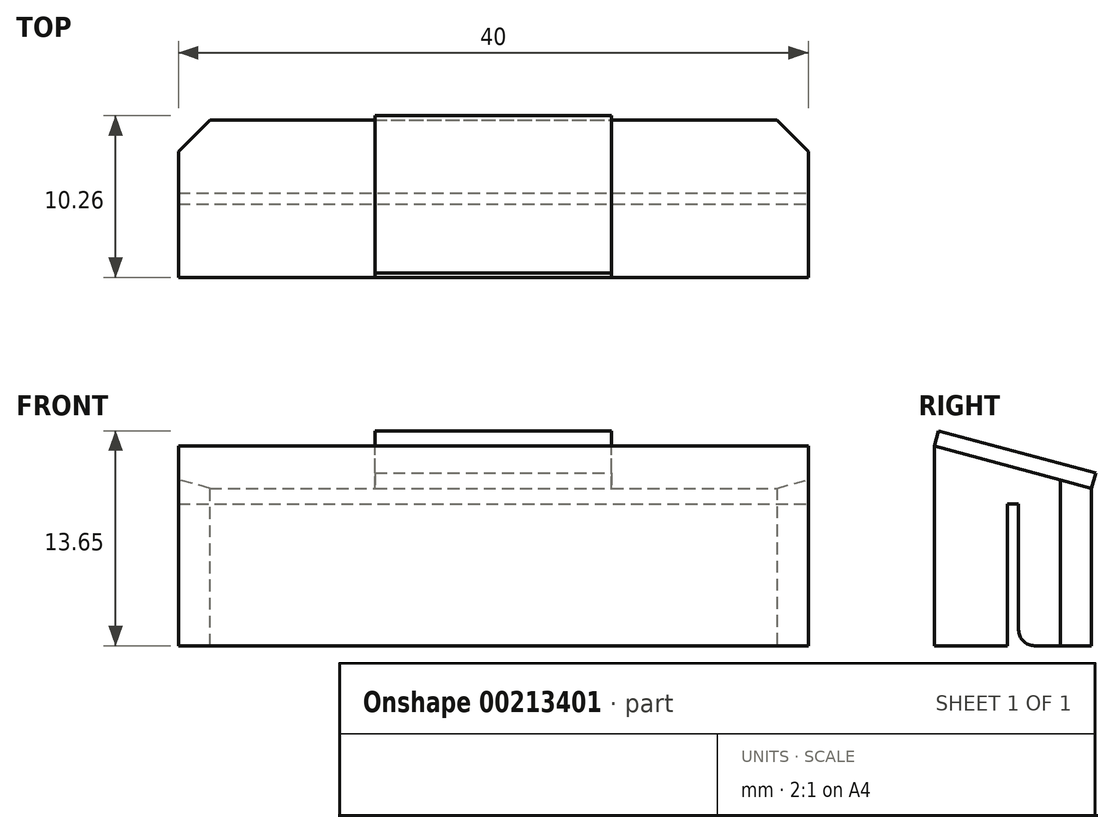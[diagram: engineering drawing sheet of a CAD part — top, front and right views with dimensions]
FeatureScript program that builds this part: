
annotation { "Feature Type Name" : "Feature", "Feature Type Description" : "" }
export const myFeature = defineFeature(function(context is Context, id is Id, definition is map)
    precondition{}
    {
        {
            var Q0;
            Q0=qCreatedBy(makeId("Top.planeOp"),FACE);
            var sketch = newSketch(context, id + "F0", { "sketchPlane" : qUnion([Q0])});
            skLineSegment(sketch, "E0.bottom", {"start": v(-20, 5) * mm, "end": v(20, 5) * mm});
            skLineSegment(sketch, "E0.top", {"start": v(-20, -5) * mm, "end": v(20, -5) * mm});
            skLineSegment(sketch, "E0.left", {"start": v(-20, 5) * mm, "end": v(-20, -5) * mm});
            skLineSegment(sketch, "E0.right", {"start": v(20, 5) * mm, "end": v(20, -5) * mm});
            skPoint(sketch, "E1", {"position": v(0, 5) * mm});
            skPoint(sketch, "E2", {"position": v(20, 0) * mm});
            skSolve(sketch);
        }
        {
            var Q0;
            Q0=makeQuery(id+"F0.imprint","IMPRINT",FACE,{"disambiguationData":[TD([[makeQuery(id+"F0.imprint","IMPRINT",EDGE,{"derivedFrom":sQuery(id+"F0.wireOp",EDGE,"E0.bottom")}),-1.0]])]});
            extrude(context, id + "F1", {"entities" : qUnion([Q0]), "depth" : 10 * mm});
        }
        {
            var Q0;
            Q0=makeQuery(id+"F1.opExtrude","SWEPT_FACE",FACE,{"disambiguationData":[OSD([sQuery(id+"F0.wireOp",EDGE,"E0.right")])]});
            var sketch = newSketch(context, id + "F2", { "sketchPlane" : qUnion([Q0])});
            skLineSegment(sketch, "E3", {"start": v(5, 10) * mm, "end": v(-5, 10) * mm});
            skLineSegment(sketch, "E4", {"start": v(-5, 10) * mm, "end": v(-5, 12.68) * mm});
            skLineSegment(sketch, "E5", {"start": v(-5, 12.68) * mm, "end": v(5, 10) * mm});
            skSolve(sketch);
        }
        {
            var Q0;
            Q0=makeQuery(id+"F2.imprint","IMPRINT",FACE,{"disambiguationData":[TD([[makeQuery(id+"F2.imprint","IMPRINT",EDGE,{"derivedFrom":sQuery(id+"F2.wireOp",EDGE,"E3")}),-1.0]])]});
            var Q1;
            Q1=makeQuery(id+"F1.opExtrude","SWEPT_FACE",FACE,{"disambiguationData":[OSD([sQuery(id+"F0.wireOp",EDGE,"E0.left")])]});
            extrude(context, id + "F3", {"entities" : qUnion([Q0]), "operationType" : NewBodyOperationType.ADD, "endBound" : BoundingType.UP_TO_SURFACE, "oppositeDirection" : true, "endBoundEntityFace" : qUnion([Q1]), "depth" : 25 * mm});
        }
        {
            var Q0;
            Q0=makeQuery(id+"F3.opExtrude","SWEPT_FACE",FACE,{"disambiguationData":[OSD([sQuery(id+"F2.wireOp",EDGE,"E5")])]});
            var sketch = newSketch(context, id + "F4", { "sketchPlane" : qUnion([Q0])});
            skLineSegment(sketch, "E6.bottom", {"start": v(-7.5, 2.24) * mm, "end": v(7.5, 2.24) * mm});
            skLineSegment(sketch, "E6.top", {"start": v(-7.5, -8.11) * mm, "end": v(7.5, -8.11) * mm});
            skLineSegment(sketch, "E6.left", {"start": v(-7.5, 2.24) * mm, "end": v(-7.5, -8.11) * mm});
            skLineSegment(sketch, "E6.right", {"start": v(7.5, 2.24) * mm, "end": v(7.5, -8.11) * mm});
            skPoint(sketch, "E7", {"position": v(0, 2.24) * mm});
            skSolve(sketch);
        }
        {
            var Q0;
            Q0=makeQuery(id+"F4.imprint","IMPRINT",FACE,{"disambiguationData":[TD([[makeQuery(id+"F4.imprint","IMPRINT",EDGE,{"derivedFrom":sQuery(id+"F4.wireOp",EDGE,"E6.bottom")}),-1.0]])]});
            extrude(context, id + "F5", {"entities" : qUnion([Q0]), "operationType" : NewBodyOperationType.ADD, "depth" : 1 * mm});
        }
        {
            var Q0;
            Q0=makeQuery(id+"F1.opExtrude","CAP_FACE",FACE,{"disambiguationData":[OSD([sQuery(id+"F0.wireOp",EDGE,"E0.bottom"),sQuery(id+"F0.wireOp",EDGE,"E0.top"),sQuery(id+"F0.wireOp",EDGE,"E0.left"),sQuery(id+"F0.wireOp",EDGE,"E0.right")])],"isStart":true});
            var sketch = newSketch(context, id + "F6", { "sketchPlane" : qUnion([Q0])});
            skLineSegment(sketch, "E8.bottom", {"start": v(-20, 0.36) * mm, "end": v(20, 0.36) * mm});
            skLineSegment(sketch, "E8.top", {"start": v(-20, -0.36) * mm, "end": v(20, -0.36) * mm});
            skLineSegment(sketch, "E8.left", {"start": v(-20, 0.36) * mm, "end": v(-20, -0.36) * mm});
            skLineSegment(sketch, "E8.right", {"start": v(20, 0.36) * mm, "end": v(20, -0.36) * mm});
            skPoint(sketch, "E9", {"position": v(-20, 0) * mm});
            skSolve(sketch);
        }
        {
            var Q0;
            Q0=makeQuery(id+"F6.imprint","IMPRINT",FACE,{"disambiguationData":[TD([[makeQuery(id+"F6.imprint","IMPRINT",EDGE,{"derivedFrom":sQuery(id+"F6.wireOp",EDGE,"E8.bottom")}),-1.0]])]});
            extrude(context, id + "F7", {"entities" : qUnion([Q0]), "operationType" : NewBodyOperationType.REMOVE, "oppositeDirection" : true, "depth" : 9 * mm});
        }
        {
            var Q0;
            Q0=makeQuery(id+"F7.boolean.opBoolean","COPY",EDGE,{"derivedFrom":makeQuery(id+"F7.opExtrude","CAP_EDGE",EDGE,{"disambiguationData":[OSD([sQuery(id+"F6.wireOp",EDGE,"E8.bottom")])],"isStart":true})});
            var Q1;
            Q1=makeQuery(id+"F7.boolean.opBoolean","COPY",EDGE,{"derivedFrom":makeQuery(id+"F7.opExtrude","CAP_EDGE",EDGE,{"disambiguationData":[OSD([sQuery(id+"F6.wireOp",EDGE,"E8.top")])],"isStart":true})});
            fillet(context, id + "F8", {"entities" : qUnion([Q0, Q1]), "radius" : 1 * mm, "tangentPropagation" : true, "allowEdgeOverflow" : false});
        }
        {
            var Q0;
            Q0=makeQuery(id+"F1.opExtrude","SWEPT_EDGE",EDGE,{"disambiguationData":[OSD([sQuery(id+"F0.wireOp",EDGE,"E0.bottom"),sQuery(id+"F0.wireOp",EDGE,"E0.right")])]});
            var Q1;
            Q1=makeQuery(id+"F1.opExtrude","SWEPT_EDGE",EDGE,{"disambiguationData":[OSD([sQuery(id+"F0.wireOp",EDGE,"E0.bottom"),sQuery(id+"F0.wireOp",EDGE,"E0.left")])]});
            chamfer(context, id + "F9", {"entities" : qUnion([Q0, Q1]), "width" : 2 * mm, "tangentPropagation" : true});
        }
    });
